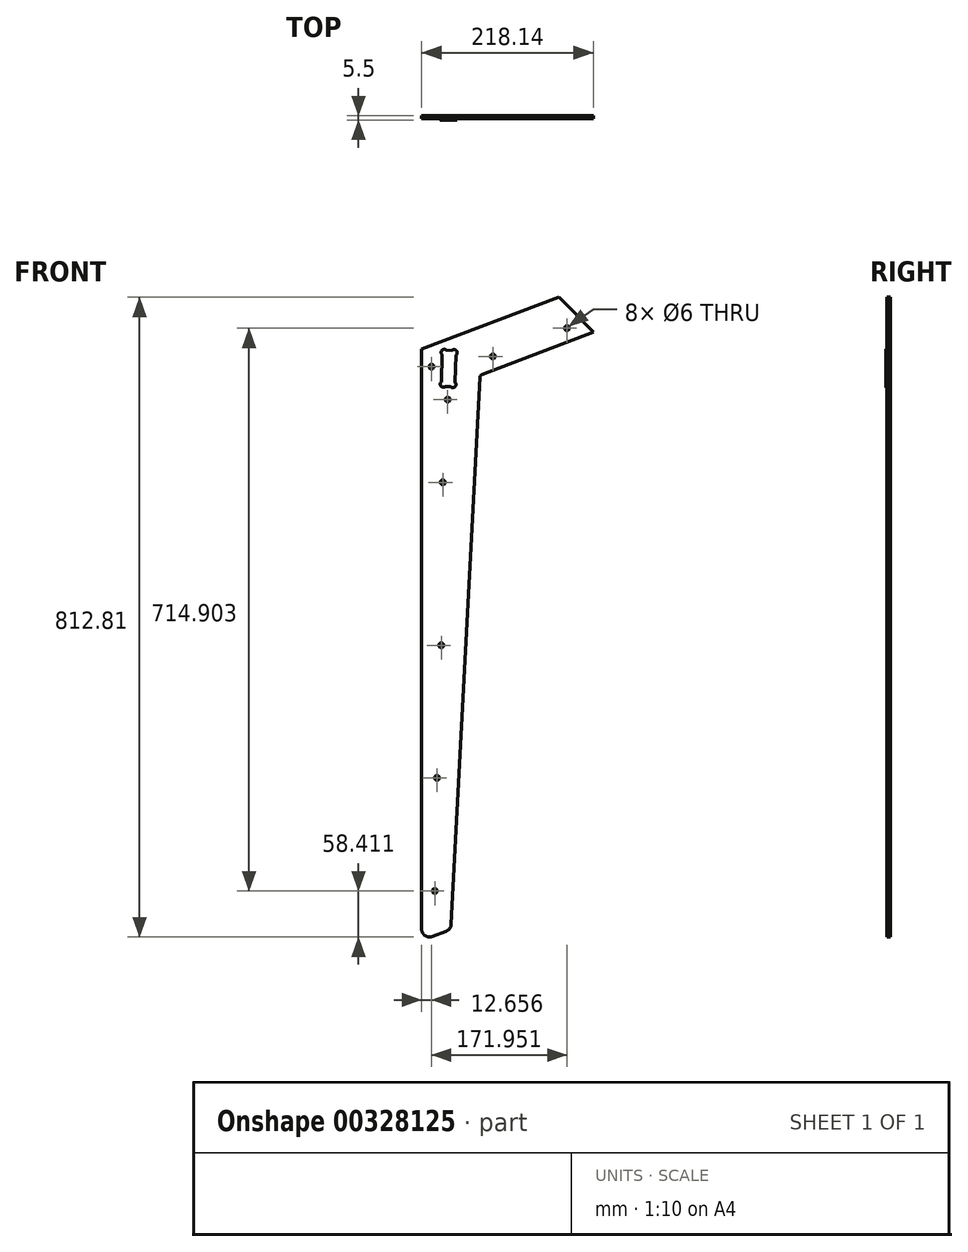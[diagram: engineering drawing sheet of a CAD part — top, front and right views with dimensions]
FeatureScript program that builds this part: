
annotation { "Feature Type Name" : "Feature", "Feature Type Description" : "" }
export const myFeature = defineFeature(function(context is Context, id is Id, definition is map)
    precondition{}
    {
        {
            var Q0;
            Q0=qCreatedBy(makeId("Front.planeOp"),FACE);
            var sketch = newSketch(context, id + "F0", { "sketchPlane" : qUnion([Q0])});
            skLineSegment(sketch, "E0", {"start": v(-101.67, -441.55) * mm, "end": v(-119.33, -448.26) * mm});
            skArc(sketch, "E1", {"start": v(-119.33, -448.26) * mm, "mid": v(-128.56, -447.15) * mm, "end": v(-132.88, -438.91) * mm});
            skLineSegment(sketch, "E2", {"start": v(-132.88, -438.91) * mm, "end": v(-132.88, 297.64) * mm});
            skLineSegment(sketch, "E3", {"start": v(-132.88, 297.64) * mm, "end": v(41.34, 363.9) * mm});
            skLineSegment(sketch, "E4", {"start": v(41.34, 363.9) * mm, "end": v(85.26, 319.44) * mm});
            skLineSegment(sketch, "E5", {"start": v(85.26, 319.44) * mm, "end": v(-56.25, 265.62) * mm});
            skArc(sketch, "E6", {"start": v(-56.25, 265.62) * mm, "mid": v(-58.06, 264.24) * mm, "end": v(-58.82, 262.09) * mm});
            skLineSegment(sketch, "E7", {"start": v(-58.82, 262.09) * mm, "end": v(-95.24, -432.72) * mm});
            skArc(sketch, "E8", {"start": v(-95.24, -432.72) * mm, "mid": v(-97.14, -438.09) * mm, "end": v(-101.67, -441.55) * mm});
            skCircle(sketch, "E9", {"center": v(-99.7, 233.75) * mm, "radius": 3 * mm});
            skCircle(sketch, "E10", {"center": v(-116.14, -390.5) * mm, "radius": 3 * mm});
            skCircle(sketch, "E11", {"center": v(-113.35, -246.7) * mm, "radius": 3 * mm});
            skCircle(sketch, "E12", {"center": v(51.73, 324.4) * mm, "radius": 3 * mm});
            skCircle(sketch, "E13", {"center": v(-120.22, 275.49) * mm, "radius": 3 * mm});
            skCircle(sketch, "E14", {"center": v(-107.92, -78.38) * mm, "radius": 3 * mm});
            skCircle(sketch, "E15", {"center": v(-105.95, 128.63) * mm, "radius": 3 * mm});
            skCircle(sketch, "E16", {"center": v(-42.35, 288.62) * mm, "radius": 3 * mm});
            skArc(sketch, "E17", {"start": v(-96.2, 250.25) * mm, "mid": v(-90.55, 250.06) * mm, "end": v(-90.38, 255.72) * mm});
            skLineSegment(sketch, "E18", {"start": v(-90.38, 255.72) * mm, "end": v(-89.01, 290.34) * mm});
            skArc(sketch, "E19", {"start": v(-89.01, 290.34) * mm, "mid": v(-88.79, 296) * mm, "end": v(-94.45, 296.2) * mm});
            skLineSegment(sketch, "E20", {"start": v(-94.45, 296.2) * mm, "end": v(-101.13, 296.44) * mm});
            skArc(sketch, "E21", {"start": v(-101.13, 296.44) * mm, "mid": v(-106.75, 296.66) * mm, "end": v(-107.03, 291.04) * mm});
            skLineSegment(sketch, "E22", {"start": v(-107.03, 291.04) * mm, "end": v(-107.9, 256.34) * mm});
            skArc(sketch, "E23", {"start": v(-107.9, 256.34) * mm, "mid": v(-108.16, 250.67) * mm, "end": v(-102.49, 250.46) * mm});
            skLineSegment(sketch, "E24", {"start": v(-102.49, 250.46) * mm, "end": v(-96.2, 250.25) * mm});
            skSolve(sketch);
        }
        {
            var Q0;
            Q0=makeQuery(id+"F0.imprint","IMPRINT",FACE,{"disambiguationData":[TD([[makeQuery(id+"F0.imprint","IMPRINT",EDGE,{"derivedFrom":sQuery(id+"F0.wireOp",EDGE,"E0")}),-1.0]])]});
            var Q1;
            Q1=makeQuery(id+"F0.imprint","IMPRINT",FACE,{"disambiguationData":[TD([[makeQuery(id+"F0.imprint","IMPRINT",EDGE,{"derivedFrom":sQuery(id+"F0.wireOp",EDGE,"E10")}),-1.0]])]});
            var Q2;
            Q2=makeQuery(id+"F0.imprint","IMPRINT",FACE,{"disambiguationData":[TD([[makeQuery(id+"F0.imprint","IMPRINT",EDGE,{"derivedFrom":sQuery(id+"F0.wireOp",EDGE,"E11")}),-1.0]])]});
            var Q3;
            Q3=makeQuery(id+"F0.imprint","IMPRINT",FACE,{"disambiguationData":[TD([[makeQuery(id+"F0.imprint","IMPRINT",EDGE,{"derivedFrom":sQuery(id+"F0.wireOp",EDGE,"E14")}),-1.0]])]});
            var Q4;
            Q4=makeQuery(id+"F0.imprint","IMPRINT",FACE,{"disambiguationData":[TD([[makeQuery(id+"F0.imprint","IMPRINT",EDGE,{"derivedFrom":sQuery(id+"F0.wireOp",EDGE,"E15")}),-1.0]])]});
            var Q5;
            Q5=makeQuery(id+"F0.imprint","IMPRINT",FACE,{"disambiguationData":[TD([[makeQuery(id+"F0.imprint","IMPRINT",EDGE,{"derivedFrom":sQuery(id+"F0.wireOp",EDGE,"E13")}),-1.0]])]});
            var Q6;
            Q6=makeQuery(id+"F0.imprint","IMPRINT",FACE,{"disambiguationData":[TD([[makeQuery(id+"F0.imprint","IMPRINT",EDGE,{"derivedFrom":sQuery(id+"F0.wireOp",EDGE,"E9")}),-1.0]])]});
            var Q7;
            Q7=makeQuery(id+"F0.imprint","IMPRINT",FACE,{"disambiguationData":[TD([[makeQuery(id+"F0.imprint","IMPRINT",EDGE,{"derivedFrom":sQuery(id+"F0.wireOp",EDGE,"E16")}),-1.0]])]});
            var Q8;
            Q8=makeQuery(id+"F0.imprint","IMPRINT",FACE,{"disambiguationData":[TD([[makeQuery(id+"F0.imprint","IMPRINT",EDGE,{"derivedFrom":sQuery(id+"F0.wireOp",EDGE,"E12")}),-1.0]])]});
            var Q9;
            Q9=makeQuery(id+"F0.imprint","IMPRINT",FACE,{"disambiguationData":[TD([[makeQuery(id+"F0.imprint","IMPRINT",EDGE,{"derivedFrom":sQuery(id+"F0.wireOp",EDGE,"E17")}),1.0]])]});
            extrude(context, id + "F1", {"entities" : qUnion([Q0, Q1, Q2, Q3, Q4, Q5, Q6, Q7, Q8, Q9]), "oppositeDirection" : true, "depth" : 18 * mm});
        }
        {
            var Q0;
            Q0=makeQuery(id+"F0.imprint","IMPRINT",FACE,{"disambiguationData":[TD([[makeQuery(id+"F0.imprint","IMPRINT",EDGE,{"derivedFrom":sQuery(id+"F0.wireOp",EDGE,"E10")}),-1.0]])]});
            var Q1;
            Q1=makeQuery(id+"F0.imprint","IMPRINT",FACE,{"disambiguationData":[TD([[makeQuery(id+"F0.imprint","IMPRINT",EDGE,{"derivedFrom":sQuery(id+"F0.wireOp",EDGE,"E11")}),-1.0]])]});
            var Q2;
            Q2=makeQuery(id+"F0.imprint","IMPRINT",FACE,{"disambiguationData":[TD([[makeQuery(id+"F0.imprint","IMPRINT",EDGE,{"derivedFrom":sQuery(id+"F0.wireOp",EDGE,"E14")}),-1.0]])]});
            var Q3;
            Q3=makeQuery(id+"F0.imprint","IMPRINT",FACE,{"disambiguationData":[TD([[makeQuery(id+"F0.imprint","IMPRINT",EDGE,{"derivedFrom":sQuery(id+"F0.wireOp",EDGE,"E15")}),-1.0]])]});
            var Q4;
            Q4=makeQuery(id+"F0.imprint","IMPRINT",FACE,{"disambiguationData":[TD([[makeQuery(id+"F0.imprint","IMPRINT",EDGE,{"derivedFrom":sQuery(id+"F0.wireOp",EDGE,"E13")}),-1.0]])]});
            var Q5;
            Q5=makeQuery(id+"F0.imprint","IMPRINT",FACE,{"disambiguationData":[TD([[makeQuery(id+"F0.imprint","IMPRINT",EDGE,{"derivedFrom":sQuery(id+"F0.wireOp",EDGE,"E9")}),-1.0]])]});
            var Q6;
            Q6=makeQuery(id+"F0.imprint","IMPRINT",FACE,{"disambiguationData":[TD([[makeQuery(id+"F0.imprint","IMPRINT",EDGE,{"derivedFrom":sQuery(id+"F0.wireOp",EDGE,"E16")}),-1.0]])]});
            var Q7;
            Q7=makeQuery(id+"F0.imprint","IMPRINT",FACE,{"disambiguationData":[TD([[makeQuery(id+"F0.imprint","IMPRINT",EDGE,{"derivedFrom":sQuery(id+"F0.wireOp",EDGE,"E12")}),-1.0]])]});
            extrude(context, id + "F2", {"entities" : qUnion([Q0, Q1, Q2, Q3, Q4, Q5, Q6, Q7]), "operationType" : NewBodyOperationType.REMOVE, "oppositeDirection" : true, "depth" : 14 * mm});
        }
        {
            var Q0;
            Q0=makeQuery(id+"F0.imprint","IMPRINT",FACE,{"disambiguationData":[TD([[makeQuery(id+"F0.imprint","IMPRINT",EDGE,{"derivedFrom":sQuery(id+"F0.wireOp",EDGE,"E17")}),1.0]])]});
            extrude(context, id + "F3", {"entities" : qUnion([Q0]), "operationType" : NewBodyOperationType.REMOVE, "oppositeDirection" : true, "depth" : 12.5 * mm});
        }
    });
